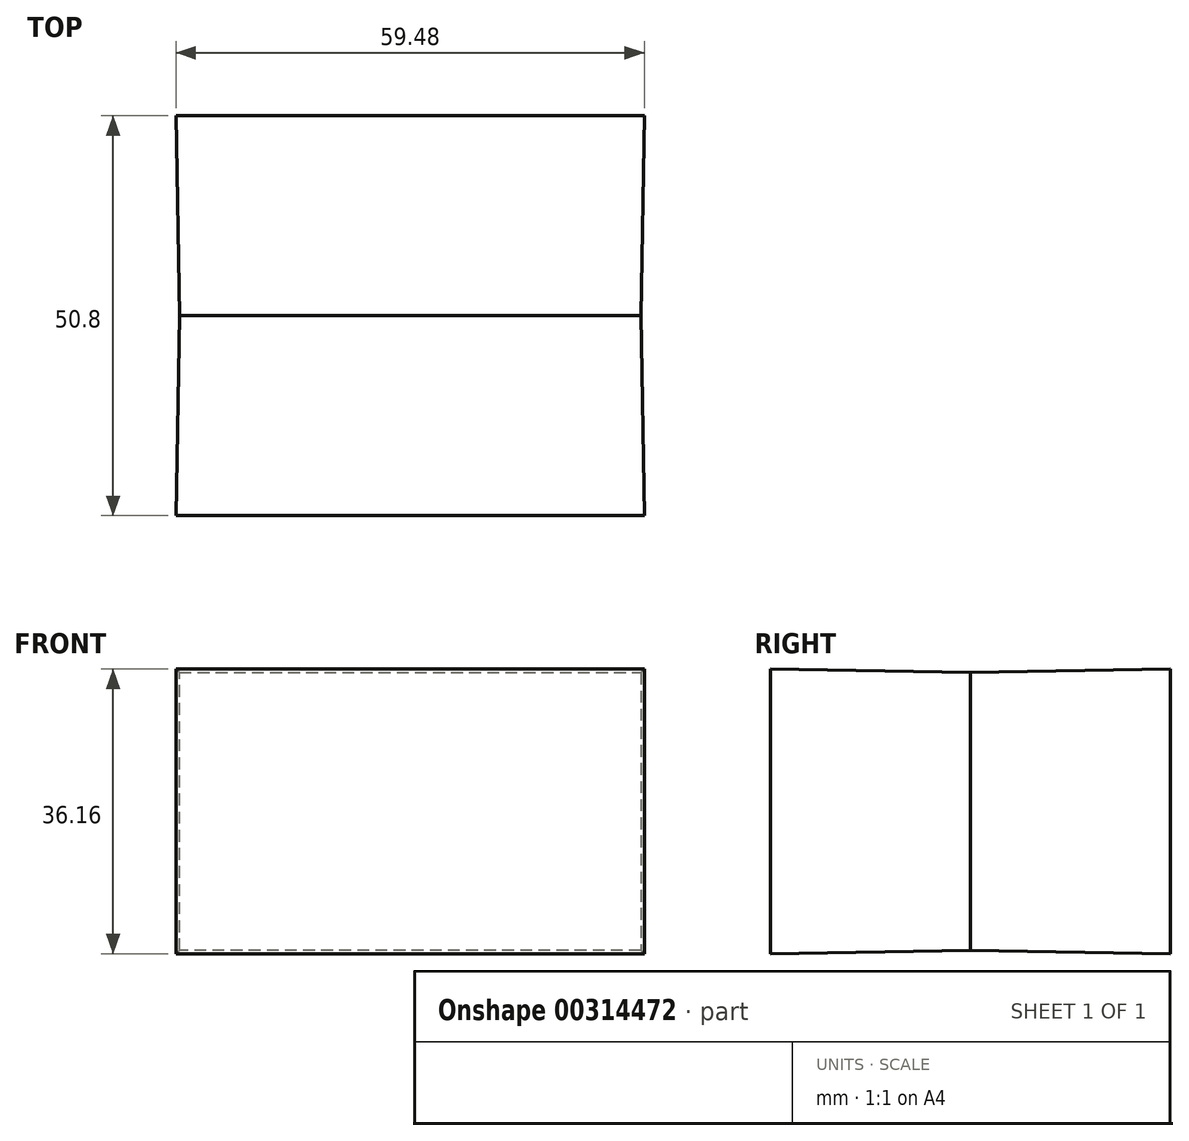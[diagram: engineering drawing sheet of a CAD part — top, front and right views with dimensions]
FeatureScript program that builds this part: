
annotation { "Feature Type Name" : "Feature", "Feature Type Description" : "" }
export const myFeature = defineFeature(function(context is Context, id is Id, definition is map)
    precondition{}
    {
        {
            var Q0;
            Q0=qCreatedBy(makeId("Front.planeOp"),FACE);
            var sketch = newSketch(context, id + "F0", { "sketchPlane" : qUnion([Q0])});
            skLineSegment(sketch, "E0.bottom", {"start": v(-29.3, 17.64) * mm, "end": v(29.3, 17.64) * mm});
            skLineSegment(sketch, "E0.top", {"start": v(-29.3, -17.64) * mm, "end": v(29.3, -17.64) * mm});
            skLineSegment(sketch, "E0.left", {"start": v(-29.3, 17.64) * mm, "end": v(-29.3, -17.64) * mm});
            skLineSegment(sketch, "E0.right", {"start": v(29.3, 17.64) * mm, "end": v(29.3, -17.64) * mm});
            skPoint(sketch, "E0.middle", {"position": v(0, 0) * mm});
            skSolve(sketch);
        }
        {
            var Q0;
            Q0 = qSketchRegion(id + "F0", true);
            extrude(context, id + "F1", {"entities" : qUnion([Q0]), "endBound" : BoundingType.SYMMETRIC, "depth" : 50.8 * mm, "hasDraft" : true, "draftAngle" : 1 * degree});
        }
    });
